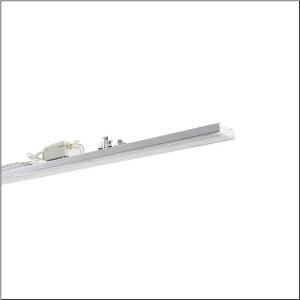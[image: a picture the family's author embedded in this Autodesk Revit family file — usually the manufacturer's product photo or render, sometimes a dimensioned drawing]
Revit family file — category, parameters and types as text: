
# Revit family: licross_r__21_recessed_mo_52te12dv4fxg3s4_28ef
name_source: partatom
category: Lighting Fixtures
units: mm (PartAtom-declared; Revit-internal decimal feet)

## family parameters
Cut with Voids When Loaded = No
Host = Face
Light Source = No
Part Type = Normal
Room Calculation Point = No
Round Connector Dimension = Use Diameter
Shared = No

## types (1)
- --- (1 x LED, 950 lm, 5.5 W, 4000K)
    Apparent Load = 6 VA
    CIE Flux Codes = 72 92 99 100 100
    Color Rendering = 80
    Color Temperature = 4000K
    Default Elevation = 1800 mm
    Description = Licross® 21 Recessed MO, luminaire insert, of sheet steel, galvanised, coil coated, white, length: 2.250mm, width: 66mm, height: 67mm, LED rated luminous flux: 15.420lm, light colour: 840, control gear: DALI 2, with plug, 6-pole, with phase selection, for trunking rail, 9 or 11-core, mains connection: 220..240V, AC, 50/60Hz, rated input power: 89W, for trunking rail, 9-/11-core, halogen-free wiring, for emergency light function, converter,control gear: single battery element, battery: LiFeP04, 9Ah, primary optical cover: cover, of PMMA, light emission: direct distribution, primary light characteristic: symmetric, protection rating (complete): IP54, insulation class (complete): insulation class I (protective earthing), certification: CE, UKCA, protection symbol: D if used in an environment with non-conductive dust loads with corresponding accessories, impact resistance: IK06, permissible ambient temperature for indoor applications: +5..+35°C, standard: EN 60598-2-22, LABS conformity tested according to VDMA 24364:2018-05, reducing of maximum allowable ambient temperature of 5°C with ceiling mounting, corresponds to IFS (International Featured Standards) requirements for safety and quality in the food industry, packaging unit: 1 piece
    Height = 58 mm
    Lamp = 1 x LED
    Lamp Light Flux = 950 lm
    Lamp Power = 5.5 W
    Lamp count = 1
    Length = 2250 mm
    Luminous efficacy = 173 lm/W
    Manufacturer = Siteco
    ModVariant = No
    Model = 52TE12DV4FXG3S4
    Mounting Place = Ceiling
    Mounting Type = Pendant
    Number of Poles = 1
    OnlyDefault = Yes
    Power Factor = 1
    Product Name = Licross® 21 Recessed MO
    Product group = luminaire insert
    ProductGroupID = 901
    Protection Class = Protection class I
    Protection Degree = IP 54
    RLX_Detail_Level = 1
    RLX_Emergency_Light_Flux = 0 lm
    RLX_Emergency_Type = 0
    RLX_Emergency_Type_DB = No
    RlxData = <blob elided: 30233 chars, md5=e72aab4b>
    Socket = socket
    Standby Power = 0 W
    System Light Flux = 950 lm
    System Power = 6 W
    Type Comments = : emergency light operation: 3 h
    Type Image = l_1296930.jpg
    URL = http://relux.com
    VarID = @adj_040189
    Voltage = 0 V
    Weight = 0.00 kg
    Width = 66 mm

## geometry (parser evidence)
native form markers: Blend x4, Sweep x9
no freeform markers — native parametric forms only
